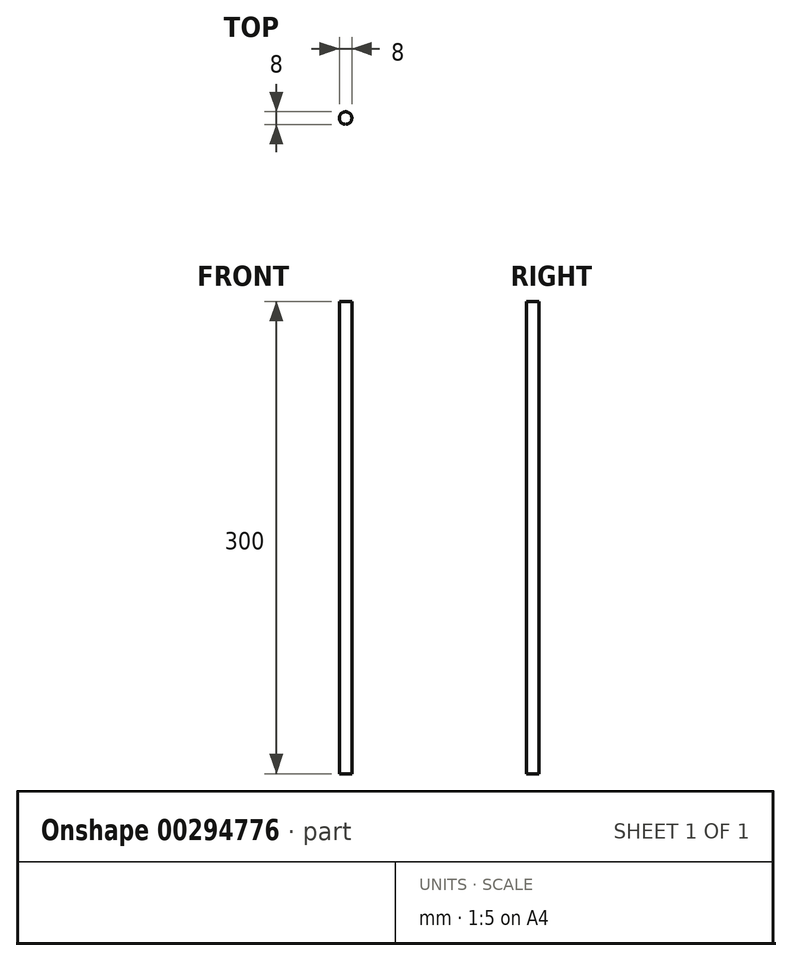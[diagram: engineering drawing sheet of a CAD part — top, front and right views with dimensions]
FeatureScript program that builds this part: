
annotation { "Feature Type Name" : "Feature", "Feature Type Description" : "" }
export const myFeature = defineFeature(function(context is Context, id is Id, definition is map)
    precondition{}
    {
        {
            var Q0;
            Q0=qCreatedBy(makeId("Top.planeOp"),FACE);
            var sketch = newSketch(context, id + "F0", { "sketchPlane" : qUnion([Q0])});
            skCircle(sketch, "E0", {"center": v(0, 0) * mm, "radius": 4 * mm});
            skSolve(sketch);
        }
        {
            var Q0;
            Q0=makeQuery(id+"F0.imprint","IMPRINT",FACE,{"disambiguationData":[TD([[makeQuery(id+"F0.imprint","IMPRINT",EDGE,{"derivedFrom":sQuery(id+"F0.wireOp",EDGE,"E0")}),1.0]])]});
            extrude(context, id + "F1", {"entities" : qUnion([Q0]), "endBound" : BoundingType.SYMMETRIC, "depth" : 300 * mm});
        }
    });
